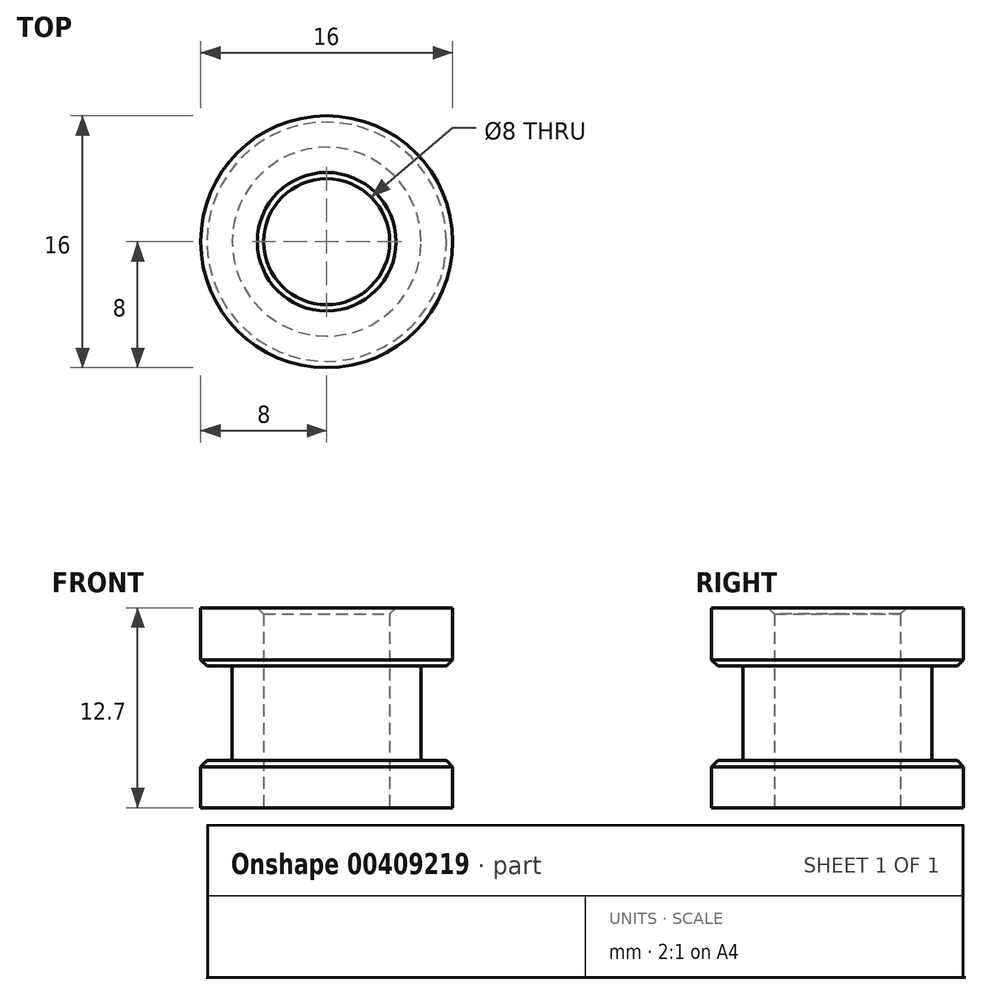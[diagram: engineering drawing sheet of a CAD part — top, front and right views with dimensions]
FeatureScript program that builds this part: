
annotation { "Feature Type Name" : "Feature", "Feature Type Description" : "" }
export const myFeature = defineFeature(function(context is Context, id is Id, definition is map)
    precondition{}
    {
        {
            var Q0;
            Q0=qCreatedBy(makeId("Front.planeOp"),FACE);
            var sketch = newSketch(context, id + "F0", { "sketchPlane" : qUnion([Q0])});
            skLineSegment(sketch, "E0", {"start": v(8, 6.7) * mm, "end": v(8, 3) * mm});
            skLineSegment(sketch, "E1", {"start": v(8, 3) * mm, "end": v(6, 3) * mm});
            skLineSegment(sketch, "E2", {"start": v(6, 3) * mm, "end": v(6, -3) * mm});
            skLineSegment(sketch, "E3", {"start": v(6, -3) * mm, "end": v(8, -3) * mm});
            skLineSegment(sketch, "E4", {"start": v(8, -3) * mm, "end": v(8, -6) * mm});
            skLineSegment(sketch, "E5", {"start": v(0, -5.39) * mm, "end": v(0, 5.39) * mm, "construction": true});
            skLineSegment(sketch, "E6", {"start": v(4, 6.7) * mm, "end": v(4, -6) * mm});
            skLineSegment(sketch, "E7", {"start": v(4, 6.7) * mm, "end": v(8, 6.7) * mm});
            skLineSegment(sketch, "E8", {"start": v(4, -6) * mm, "end": v(8, -6) * mm});
            skSolve(sketch);
        }
        {
            var Q0;
            Q0 = qSketchRegion(id + "F0", true);
            var Q1;
            Q1=sQuery(id+"F0.wireOp",EDGE,"E5");
            revolve(context, id + "F1", {"entities" : qUnion([Q0]), "axis" : qUnion([Q1]), "revolveType" : RevolveType.FULL});
        }
        {
            var Q0;
            Q0=makeQuery(id+"F1.opRevolve","SWEPT_EDGE",EDGE,{"disambiguationData":[OSD([sQuery(id+"F0.wireOp",EDGE,"E0"),sQuery(id+"F0.wireOp",EDGE,"E1")])]});
            var Q1;
            Q1=makeQuery(id+"F1.opRevolve","SWEPT_EDGE",EDGE,{"disambiguationData":[OSD([sQuery(id+"F0.wireOp",EDGE,"E3"),sQuery(id+"F0.wireOp",EDGE,"E4")])]});
            var Q2;
            Q2=makeQuery(id+"F1.opRevolve","SWEPT_EDGE",EDGE,{"disambiguationData":[OSD([sQuery(id+"F0.wireOp",EDGE,"E6"),sQuery(id+"F0.wireOp",EDGE,"E7")])]});
            chamfer(context, id + "F2", {"entities" : qUnion([Q0, Q1, Q2]), "width" : 0.4 * mm, "tangentPropagation" : true});
        }
    });
